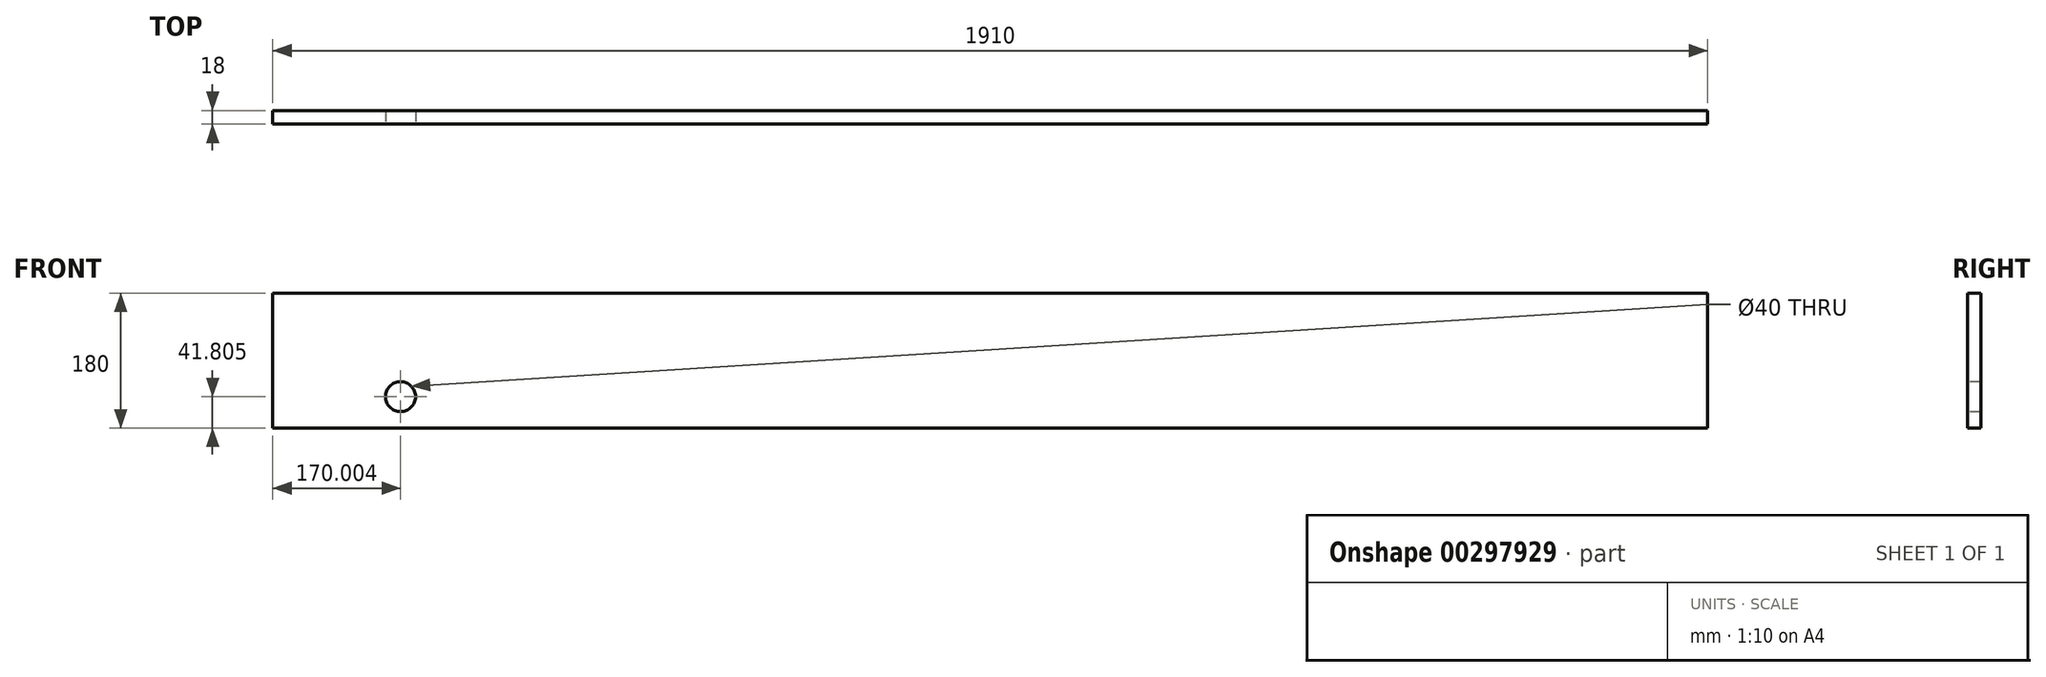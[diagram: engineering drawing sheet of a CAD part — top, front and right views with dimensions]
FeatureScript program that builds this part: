
annotation { "Feature Type Name" : "Feature", "Feature Type Description" : "" }
export const myFeature = defineFeature(function(context is Context, id is Id, definition is map)
    precondition{}
    {
        {
            var Q0;
            Q0=qCreatedBy(makeId("Front.planeOp"),FACE);
            var sketch = newSketch(context, id + "F0", { "sketchPlane" : qUnion([Q0])});
            skLineSegment(sketch, "E0.bottom", {"start": v(-619.2, 37.58) * mm, "end": v(1290.8, 37.58) * mm});
            skLineSegment(sketch, "E0.top", {"start": v(-619.2, -142.42) * mm, "end": v(1290.8, -142.42) * mm});
            skLineSegment(sketch, "E0.left", {"start": v(-619.2, 37.58) * mm, "end": v(-619.2, -142.42) * mm});
            skLineSegment(sketch, "E0.right", {"start": v(1290.8, 37.58) * mm, "end": v(1290.8, -142.42) * mm});
            skSolve(sketch);
        }
        {
            var Q0;
            Q0=makeQuery(id+"F0.imprint","IMPRINT",FACE,{"disambiguationData":[TD([[makeQuery(id+"F0.imprint","IMPRINT",EDGE,{"derivedFrom":sQuery(id+"F0.wireOp",EDGE,"E0.bottom")}),-1.0]])]});
            extrude(context, id + "F1", {"entities" : qUnion([Q0]), "endBound" : BoundingType.SYMMETRIC, "depth" : 18 * mm});
        }
        {
            var Q0;
            Q0=makeQuery(id+"F1.opExtrude","CAP_FACE",FACE,{"disambiguationData":[OSD([sQuery(id+"F0.wireOp",EDGE,"E0.bottom"),sQuery(id+"F0.wireOp",EDGE,"E0.top"),sQuery(id+"F0.wireOp",EDGE,"E0.left"),sQuery(id+"F0.wireOp",EDGE,"E0.right")])],"isStart":false});
            var sketch = newSketch(context, id + "F2", { "sketchPlane" : qUnion([Q0])});
            skCircle(sketch, "E1", {"center": v(-449.2, -100.62) * mm, "radius": 20 * mm});
            skSolve(sketch);
        }
        {
            var Q0;
            Q0=makeQuery(id+"F2.imprint","IMPRINT",FACE,{"disambiguationData":[TD([[makeQuery(id+"F2.imprint","IMPRINT",EDGE,{"derivedFrom":sQuery(id+"F2.wireOp",EDGE,"E1")}),1.0]])]});
            extrude(context, id + "F3", {"entities" : qUnion([Q0]), "operationType" : NewBodyOperationType.REMOVE, "oppositeDirection" : true, "depth" : 25 * mm});
        }
    });
